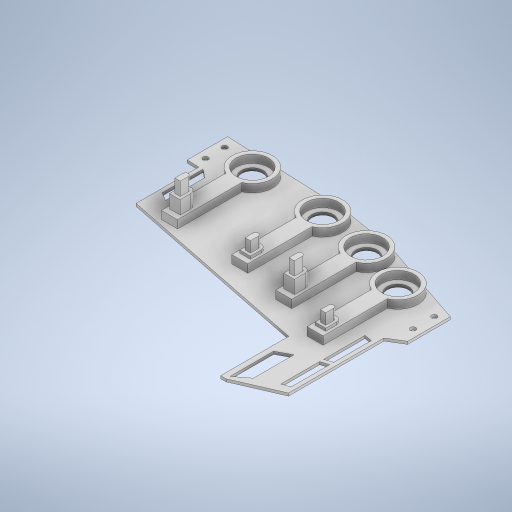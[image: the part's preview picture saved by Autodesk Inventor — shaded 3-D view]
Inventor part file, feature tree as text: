
AUTODESK INVENTOR PART (.ipt)
format: ipt  version: 2023 (Build 270158000, 158)  size: 9,900,032 bytes
history: native  units: mm
features: extrude x7, other x3, sketch x1
ambient origin geometry x8: Origin, YZ Plane, XZ Plane, XY Plane, X Axis, Y Axis, Z Axis, Center Point
bodies: Solid1 (feature_tree)
feature tree (11):
  sketch  "Sketch1"  dims[d1=205.0mm d2=85.0mm d3=85.0mm d11=225.0mm d14=85.0mm d19=40.0mm d20=40.0mm d21=61.0mm d25=215.0mm d49=12.1mm d50=12.1mm d51=12.1mm d61=1.0mm d62=0.0mm d70=15.1mm d71=15.1mm d74=25.0mm d75=2.0mm d76=2.0mm d77=3.0mm d97=25.0mm d98=2.0mm d99=2.0mm d100=3.0mm d111=8.0mm d113=8.0mm d132=534.617186mm d136=1.175916mm d137=3.273492mm d142=1.5mm d143=14.5mm d144=1.5mm d145=14.5mm d146=1.5mm d147=1.5mm d148=2.0mm d152=8.0mm d153=0.0mm d154=3.0mm d155=0.0mm d159=4.0mm d160=4.0mm d161=4.0mm d168=4.0mm d169=4.0mm d170=4.0mm d180=4.0mm d181=0.0mm d215=12.1mm d216=15.1mm d217=25.0mm d218=2.0mm d219=2.0mm d220=3.0mm d221=8.0mm d234=6.0mm d235=4.0mm d242=4.0mm d243=4.0mm d244=4.0mm d248=6.0mm d249=4.0mm d250=4.0mm d251=2.0mm d252=2.0mm d253=4.0mm d254=6.0mm d255=4.0mm d256=4.0mm d257=2.0mm d258=2.0mm d259=1.5mm d260=1.5mm d264=25.0mm d265=2.0mm d266=2.0mm d267=3.0mm d268=4.0mm d269=4.0mm d270=4.0mm d274=8.0mm d281=6.0mm d282=6.0mm d283=6.0mm d284=6.0mm d285=6.0mm d286=6.0mm d287=6.0mm d288=6.0mm d292=6.0mm d293=6.0mm d294=6.0mm d295=6.0mm d299=6.0mm d300=6.0mm d301=6.0mm d302=6.0mm d306=3.0mm d307=0.0mm d308=13.0mm d309=0.0mm d310=8.0mm d311=0.0mm d312=0.5mm d313=0.872665mm]
  extrude  "Extrusion1"  Depth=8.0mm
  extrude  "Extrusion3"  Depth=8.0mm
  extrude  "Extrusion2"  Depth=8.0mm
  extrude  "Extrusion4"  Depth=8.0mm
  extrude  "Extrusion5"  Depth=8.0mm
  extrude  "Extrusion6"  Depth=8.0mm
  extrude  "Extrusion7"  Depth=8.0mm
  other  "Image1"
  other  "Image2"
  other  "Image3"
